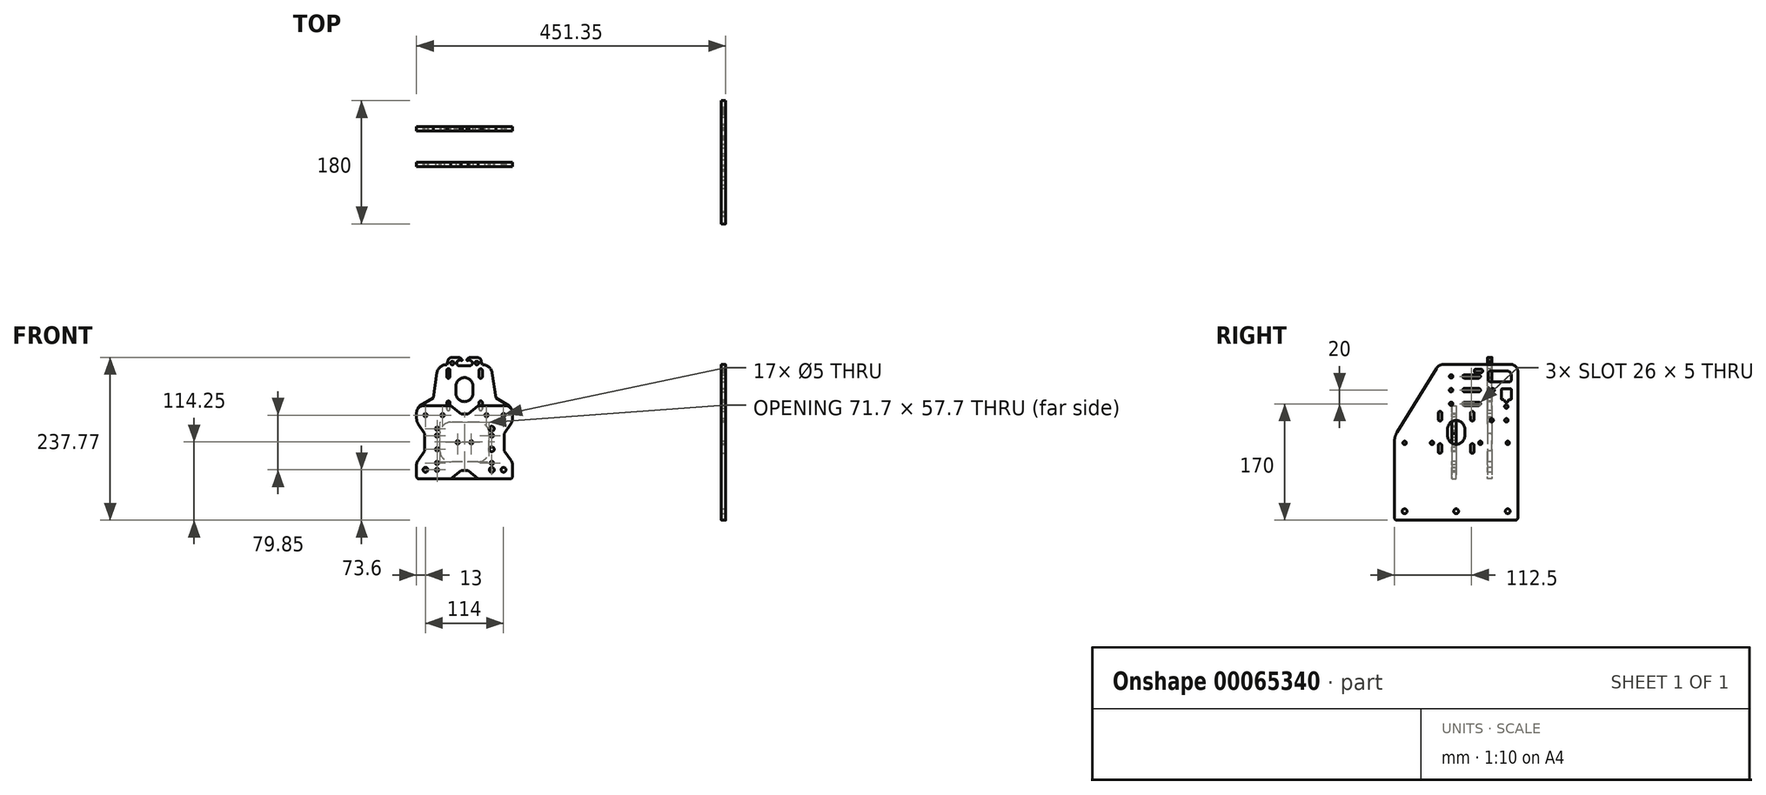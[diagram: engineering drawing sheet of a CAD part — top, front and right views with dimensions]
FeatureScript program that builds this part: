
annotation { "Feature Type Name" : "Feature", "Feature Type Description" : "" }
export const myFeature = defineFeature(function(context is Context, id is Id, definition is map)
    precondition{}
    {
        {
            var Q0;
            Q0=qCreatedBy(makeId("Right.planeOp"),FACE);
            var sketch = newSketch(context, id + "F0", { "sketchPlane" : qUnion([Q0])});
            skLineSegment(sketch, "E0", {"start": v(-28.77, 108.05) * mm, "end": v(-86.28, 14.78) * mm});
            skLineSegment(sketch, "E1", {"start": v(-90, 1.66) * mm, "end": v(-90, -110.25) * mm});
            skLineSegment(sketch, "E2", {"start": v(-86.5, -113.75) * mm, "end": v(86.5, -113.75) * mm});
            skLineSegment(sketch, "E3", {"start": v(90, -110.25) * mm, "end": v(90, 103.75) * mm});
            skLineSegment(sketch, "E4", {"start": v(80, 113.75) * mm, "end": v(-18.55, 113.75) * mm});
            skLineSegment(sketch, "E5", {"start": v(0, -113.75) * mm, "end": v(0, 0) * mm, "construction": true});
            skLineSegment(sketch, "E6", {"start": v(0, 0) * mm, "end": v(0, 113.75) * mm, "construction": true});
            skPoint(sketch, "E7.visualSharp", {"position": v(-25.25, 113.75) * mm});
            skArc(sketch, "E7.filletArc", {"start": v(-18.55, 113.75) * mm, "mid": v(-24.4, 112.23) * mm, "end": v(-28.77, 108.05) * mm});
            skPoint(sketch, "E8.visualSharp", {"position": v(90, 113.75) * mm});
            skArc(sketch, "E8.filletArc", {"start": v(90, 103.75) * mm, "mid": v(87.07, 110.82) * mm, "end": v(80, 113.75) * mm});
            skPoint(sketch, "E9.visualSharp", {"position": v(-90, -113.75) * mm});
            skArc(sketch, "E9.filletArc", {"start": v(-90, -110.25) * mm, "mid": v(-88.97, -112.72) * mm, "end": v(-86.5, -113.75) * mm});
            skPoint(sketch, "E10.visualSharp", {"position": v(90, -113.75) * mm});
            skArc(sketch, "E10.filletArc", {"start": v(86.5, -113.75) * mm, "mid": v(88.97, -112.72) * mm, "end": v(90, -110.25) * mm});
            skPoint(sketch, "E11.visualSharp", {"position": v(-90, 8.75) * mm});
            skArc(sketch, "E11.filletArc", {"start": v(-86.28, 14.78) * mm, "mid": v(-89.05, 8.48) * mm, "end": v(-90, 1.66) * mm});
            skSolve(sketch);
        }
        {
            var Q0;
            Q0=qSketchRegion(id+"F0",true);
            extrude(context, id + "F1", {"entities" : qUnion([Q0]), "depth" : 6.35 * mm});
        }
        {
            var Q0;
            Q0=makeQuery(id+"F1.opExtrude","CAP_FACE",FACE,{"disambiguationData":[OSD([sQuery(id+"F0.wireOp",EDGE,"E0"),sQuery(id+"F0.wireOp",EDGE,"E1"),sQuery(id+"F0.wireOp",EDGE,"E2"),sQuery(id+"F0.wireOp",EDGE,"E3"),sQuery(id+"F0.wireOp",EDGE,"E4"),sQuery(id+"F0.wireOp",EDGE,"E7.filletArc"),sQuery(id+"F0.wireOp",EDGE,"E8.filletArc"),sQuery(id+"F0.wireOp",EDGE,"E9.filletArc"),sQuery(id+"F0.wireOp",EDGE,"E10.filletArc"),sQuery(id+"F0.wireOp",EDGE,"E11.filletArc")])],"isStart":false});
            var sketch = newSketch(context, id + "F2", { "sketchPlane" : qUnion([Q0])});
            skLineSegment(sketch, "E12", {"start": v(0, 0) * mm, "end": v(0, -100.75) * mm, "construction": true});
            skLineSegment(sketch, "E13", {"start": v(0, -100.75) * mm, "end": v(75.3, -100.75) * mm, "construction": true});
            skLineSegment(sketch, "E14", {"start": v(0, -100.75) * mm, "end": v(-75.3, -100.75) * mm, "construction": true});
            skCircle(sketch, "E15", {"center": v(-75.3, -100.75) * mm, "radius": 3.57 * mm});
            skCircle(sketch, "E16", {"center": v(75.3, -100.75) * mm, "radius": 3.57 * mm});
            skCircle(sketch, "E17", {"center": v(0, -100.75) * mm, "radius": 3.57 * mm});
            skLineSegment(sketch, "E18", {"start": v(-75.3, -0.75) * mm, "end": v(-35.3, -0.75) * mm, "construction": true});
            skLineSegment(sketch, "E19", {"start": v(-35.3, -0.75) * mm, "end": v(0, -0.75) * mm, "construction": true});
            skLineSegment(sketch, "E20", {"start": v(0, -0.75) * mm, "end": v(35.3, -0.75) * mm, "construction": true});
            skLineSegment(sketch, "E21", {"start": v(35.3, -0.75) * mm, "end": v(75.3, -0.75) * mm, "construction": true});
            skCircle(sketch, "E22", {"center": v(-75.3, -0.75) * mm, "radius": 2.5 * mm});
            skCircle(sketch, "E23", {"center": v(-35.3, -0.75) * mm, "radius": 2.5 * mm});
            skCircle(sketch, "E24", {"center": v(35.3, -0.75) * mm, "radius": 2.5 * mm});
            skCircle(sketch, "E25", {"center": v(75.3, -0.75) * mm, "radius": 2.5 * mm});
            skLineSegment(sketch, "E26", {"start": v(-75.3, -0.75) * mm, "end": v(-75.3, -100.75) * mm, "construction": true});
            skLineSegment(sketch, "E27", {"start": v(75.3, -0.75) * mm, "end": v(75.3, -100.75) * mm, "construction": true});
            skSolve(sketch);
        }
        {
            var Q0;
            Q0=qSketchRegion(id+"F2",true);
            extrude(context, id + "F3", {"entities" : qUnion([Q0]), "operationType" : NewBodyOperationType.REMOVE, "endBound" : BoundingType.THROUGH_ALL, "oppositeDirection" : true, "depth" : 25 * mm});
        }
        {
            var Q0;
            Q0=makeQuery(id+"F1.opExtrude","CAP_FACE",FACE,{"disambiguationData":[OSD([sQuery(id+"F0.wireOp",EDGE,"E0"),sQuery(id+"F0.wireOp",EDGE,"E1"),sQuery(id+"F0.wireOp",EDGE,"E2"),sQuery(id+"F0.wireOp",EDGE,"E3"),sQuery(id+"F0.wireOp",EDGE,"E4"),sQuery(id+"F0.wireOp",EDGE,"E7.filletArc"),sQuery(id+"F0.wireOp",EDGE,"E8.filletArc"),sQuery(id+"F0.wireOp",EDGE,"E9.filletArc"),sQuery(id+"F0.wireOp",EDGE,"E10.filletArc"),sQuery(id+"F0.wireOp",EDGE,"E11.filletArc")])],"isStart":false});
            var sketch = newSketch(context, id + "F4", { "sketchPlane" : qUnion([Q0])});
            skArc(sketch, "E28", {"start": v(-12.5, 9.55) * mm, "mid": v(0, -2.95) * mm, "end": v(12.5, 9.55) * mm});
            skLineSegment(sketch, "E29", {"start": v(-12.5, 9.55) * mm, "end": v(-12.5, 19.55) * mm});
            skLineSegment(sketch, "E30", {"start": v(12.5, 19.55) * mm, "end": v(12.5, 9.55) * mm});
            skArc(sketch, "E31", {"start": v(-12.5, 19.55) * mm, "mid": v(0, 32.05) * mm, "end": v(12.5, 19.55) * mm});
            skLineSegment(sketch, "E32", {"start": v(0, 19.55) * mm, "end": v(0, 9.55) * mm, "construction": true});
            skLineSegment(sketch, "E33", {"start": v(-35.3, -0.75) * mm, "end": v(35.3, -0.75) * mm, "construction": true});
            skLineSegment(sketch, "E34", {"start": v(-23.57, 42.62) * mm, "end": v(-23.57, 33.62) * mm, "construction": true});
            skArc(sketch, "E35", {"start": v(-21.02, 42.62) * mm, "mid": v(-23.57, 45.17) * mm, "end": v(-26.12, 42.62) * mm});
            skArc(sketch, "E36", {"start": v(-26.12, 33.62) * mm, "mid": v(-23.57, 31.07) * mm, "end": v(-21.02, 33.62) * mm});
            skLineSegment(sketch, "E37", {"start": v(-21.02, 42.62) * mm, "end": v(-21.02, 33.62) * mm});
            skLineSegment(sketch, "E38", {"start": v(-26.12, 33.62) * mm, "end": v(-26.12, 42.62) * mm});
            skLineSegment(sketch, "E39", {"start": v(-12.5, 14.55) * mm, "end": v(12.5, 14.55) * mm, "construction": true});
            skLineSegment(sketch, "E40.MirrorCS", {"start": v(23.57, 42.62) * mm, "end": v(23.57, 33.62) * mm, "construction": true});
            skArc(sketch, "E41.MirrorCS", {"start": v(26.12, 33.62) * mm, "mid": v(23.57, 31.07) * mm, "end": v(21.02, 33.62) * mm});
            skLineSegment(sketch, "E42.MirrorCS", {"start": v(21.02, 42.62) * mm, "end": v(21.02, 33.62) * mm});
            skArc(sketch, "E43.MirrorCS", {"start": v(21.02, 42.62) * mm, "mid": v(23.57, 45.17) * mm, "end": v(26.12, 42.62) * mm});
            skLineSegment(sketch, "E44.MirrorCS", {"start": v(26.12, 33.62) * mm, "end": v(26.12, 42.62) * mm});
            skArc(sketch, "E45.MirrorCS", {"start": v(26.12, -4.52) * mm, "mid": v(23.57, -1.97) * mm, "end": v(21.02, -4.52) * mm});
            skLineSegment(sketch, "E46.MirrorCS", {"start": v(26.12, -4.52) * mm, "end": v(26.12, -13.52) * mm});
            skLineSegment(sketch, "E47.MirrorCS", {"start": v(-23.57, -13.52) * mm, "end": v(-23.57, -4.52) * mm, "construction": true});
            skLineSegment(sketch, "E48.MirrorCS", {"start": v(23.57, -13.52) * mm, "end": v(23.57, -4.52) * mm, "construction": true});
            skArc(sketch, "E49.MirrorCS", {"start": v(21.02, -13.52) * mm, "mid": v(23.57, -16.07) * mm, "end": v(26.12, -13.52) * mm});
            skLineSegment(sketch, "E50.MirrorCS", {"start": v(21.02, -13.52) * mm, "end": v(21.02, -4.52) * mm});
            skArc(sketch, "E51.MirrorCS", {"start": v(-26.12, -4.52) * mm, "mid": v(-23.57, -1.97) * mm, "end": v(-21.02, -4.52) * mm});
            skLineSegment(sketch, "E52.MirrorCS", {"start": v(-21.02, -13.52) * mm, "end": v(-21.02, -4.52) * mm});
            skArc(sketch, "E53.MirrorCS", {"start": v(-21.02, -13.52) * mm, "mid": v(-23.57, -16.07) * mm, "end": v(-26.12, -13.52) * mm});
            skLineSegment(sketch, "E54.MirrorCS", {"start": v(-26.12, -4.52) * mm, "end": v(-26.12, -13.52) * mm});
            skLineSegment(sketch, "E55", {"start": v(-23.57, 38.12) * mm, "end": v(23.57, -9.02) * mm, "construction": true});
            skLineSegment(sketch, "E56", {"start": v(23.57, -9.02) * mm, "end": v(-23.57, -9.02) * mm, "construction": true});
            skLineSegment(sketch, "E57", {"start": v(-23.57, -9.02) * mm, "end": v(23.57, 38.12) * mm, "construction": true});
            skSolve(sketch);
        }
        {
            var Q0;
            Q0=qSketchRegion(id+"F4",true);
            extrude(context, id + "F5", {"entities" : qUnion([Q0]), "operationType" : NewBodyOperationType.REMOVE, "endBound" : BoundingType.THROUGH_ALL, "oppositeDirection" : true, "depth" : 25 * mm});
        }
        {
            var Q0;
            Q0=makeQuery(id+"F1.opExtrude","CAP_FACE",FACE,{"disambiguationData":[OSD([sQuery(id+"F0.wireOp",EDGE,"E0"),sQuery(id+"F0.wireOp",EDGE,"E1"),sQuery(id+"F0.wireOp",EDGE,"E2"),sQuery(id+"F0.wireOp",EDGE,"E3"),sQuery(id+"F0.wireOp",EDGE,"E4"),sQuery(id+"F0.wireOp",EDGE,"E7.filletArc"),sQuery(id+"F0.wireOp",EDGE,"E8.filletArc"),sQuery(id+"F0.wireOp",EDGE,"E9.filletArc"),sQuery(id+"F0.wireOp",EDGE,"E10.filletArc"),sQuery(id+"F0.wireOp",EDGE,"E11.filletArc")])],"isStart":false});
            var sketch = newSketch(context, id + "F6", { "sketchPlane" : qUnion([Q0])});
            skCircle(sketch, "E58", {"center": v(-7.35, 96.25) * mm, "radius": 2.5 * mm});
            skLineSegment(sketch, "E59", {"start": v(-7.35, 96.25) * mm, "end": v(12, 96.25) * mm, "construction": true});
            skLineSegment(sketch, "E60", {"start": v(12, 96.25) * mm, "end": v(33, 96.25) * mm, "construction": true});
            skArc(sketch, "E61", {"start": v(12, 93.75) * mm, "mid": v(9.5, 96.25) * mm, "end": v(12, 98.75) * mm});
            skArc(sketch, "E62", {"start": v(33, 98.75) * mm, "mid": v(35.5, 96.25) * mm, "end": v(33, 93.75) * mm});
            skLineSegment(sketch, "E63", {"start": v(12, 98.75) * mm, "end": v(33, 98.75) * mm});
            skLineSegment(sketch, "E64", {"start": v(12, 93.75) * mm, "end": v(33, 93.75) * mm});
            skCircle(sketch, "E65.0.1.0", {"center": v(-7.35, 76.25) * mm, "radius": 2.5 * mm});
            skLineSegment(sketch, "E65.0.1.1", {"start": v(-7.35, 76.25) * mm, "end": v(12, 76.25) * mm, "construction": true});
            skArc(sketch, "E65.0.1.2", {"start": v(12, 73.75) * mm, "mid": v(9.5, 76.25) * mm, "end": v(12, 78.75) * mm});
            skLineSegment(sketch, "E65.0.1.3", {"start": v(12, 78.75) * mm, "end": v(33, 78.75) * mm});
            skLineSegment(sketch, "E65.0.1.4", {"start": v(12, 73.75) * mm, "end": v(33, 73.75) * mm});
            skArc(sketch, "E65.0.1.5", {"start": v(33, 78.75) * mm, "mid": v(35.5, 76.25) * mm, "end": v(33, 73.75) * mm});
            skCircle(sketch, "E65.0.2.0", {"center": v(-7.35, 56.25) * mm, "radius": 2.5 * mm});
            skLineSegment(sketch, "E65.0.2.1", {"start": v(-7.35, 56.25) * mm, "end": v(12, 56.25) * mm, "construction": true});
            skArc(sketch, "E65.0.2.2", {"start": v(12, 53.75) * mm, "mid": v(9.5, 56.25) * mm, "end": v(12, 58.75) * mm});
            skLineSegment(sketch, "E65.0.2.3", {"start": v(12, 58.75) * mm, "end": v(33, 58.75) * mm});
            skLineSegment(sketch, "E65.0.2.4", {"start": v(12, 53.75) * mm, "end": v(33, 53.75) * mm});
            skArc(sketch, "E65.0.2.5", {"start": v(33, 58.75) * mm, "mid": v(35.5, 56.25) * mm, "end": v(33, 53.75) * mm});
            skLineSegment(sketch, "E65.direction1", {"start": v(-7.35, 96.25) * mm, "end": v(-7.35, 96.25) * mm});
            skLineSegment(sketch, "E65.direction2", {"start": v(-7.35, 96.25) * mm, "end": v(-7.35, 76.25) * mm, "construction": true});
            skLineSegment(sketch, "E66", {"start": v(33, 76.25) * mm, "end": v(12, 76.25) * mm, "construction": true});
            skLineSegment(sketch, "E67", {"start": v(12, 56.25) * mm, "end": v(33, 56.25) * mm, "construction": true});
            skLineSegment(sketch, "E68", {"start": v(33, 76.25) * mm, "end": v(53.35, 76.25) * mm, "construction": true});
            skPoint(sketch, "E68.endSnap0", {"position": v(35.5, 76.25) * mm});
            skCircle(sketch, "E69", {"center": v(53.35, 76.25) * mm, "radius": 2.5 * mm});
            skSolve(sketch);
        }
        {
            var Q0;
            Q0=qSketchRegion(id+"F6",true);
            extrude(context, id + "F7", {"entities" : qUnion([Q0]), "operationType" : NewBodyOperationType.REMOVE, "endBound" : BoundingType.THROUGH_ALL, "oppositeDirection" : true, "depth" : 25 * mm});
        }
        {
            var Q0;
            Q0=makeQuery(id+"F1.opExtrude","CAP_FACE",FACE,{"disambiguationData":[OSD([sQuery(id+"F0.wireOp",EDGE,"E0"),sQuery(id+"F0.wireOp",EDGE,"E1"),sQuery(id+"F0.wireOp",EDGE,"E2"),sQuery(id+"F0.wireOp",EDGE,"E3"),sQuery(id+"F0.wireOp",EDGE,"E4"),sQuery(id+"F0.wireOp",EDGE,"E7.filletArc"),sQuery(id+"F0.wireOp",EDGE,"E8.filletArc"),sQuery(id+"F0.wireOp",EDGE,"E9.filletArc"),sQuery(id+"F0.wireOp",EDGE,"E10.filletArc"),sQuery(id+"F0.wireOp",EDGE,"E11.filletArc")])],"isStart":false});
            var sketch = newSketch(context, id + "F8", { "sketchPlane" : qUnion([Q0])});
            skLineSegment(sketch, "E70", {"start": v(12, 96.25) * mm, "end": v(33, 96.25) * mm, "construction": true});
            skLineSegment(sketch, "E71.bottom", {"start": v(28.1, 106.75) * mm, "end": v(36.9, 106.75) * mm});
            skLineSegment(sketch, "E71.top", {"start": v(28.1, 101.75) * mm, "end": v(36.9, 101.75) * mm});
            skLineSegment(sketch, "E71.left", {"start": v(26.5, 105.15) * mm, "end": v(26.5, 103.35) * mm});
            skLineSegment(sketch, "E71.right", {"start": v(38.5, 105.15) * mm, "end": v(38.5, 103.35) * mm});
            skPoint(sketch, "E72.visualSharp", {"position": v(26.5, 101.75) * mm});
            skArc(sketch, "E72.filletArc", {"start": v(26.5, 103.35) * mm, "mid": v(26.97, 102.22) * mm, "end": v(28.1, 101.75) * mm});
            skPoint(sketch, "E73.visualSharp", {"position": v(26.5, 106.75) * mm});
            skArc(sketch, "E73.filletArc", {"start": v(28.1, 106.75) * mm, "mid": v(26.97, 106.28) * mm, "end": v(26.5, 105.15) * mm});
            skPoint(sketch, "E74.visualSharp", {"position": v(38.5, 106.75) * mm});
            skArc(sketch, "E74.filletArc", {"start": v(38.5, 105.15) * mm, "mid": v(38.03, 106.28) * mm, "end": v(36.9, 106.75) * mm});
            skPoint(sketch, "E75.visualSharp", {"position": v(38.5, 101.75) * mm});
            skArc(sketch, "E75.filletArc", {"start": v(36.9, 101.75) * mm, "mid": v(38.03, 102.22) * mm, "end": v(38.5, 103.35) * mm});
            skLineSegment(sketch, "E76", {"start": v(26.5, 104.25) * mm, "end": v(38.5, 104.25) * mm, "construction": true});
            skLineSegment(sketch, "E77", {"start": v(32.5, 106.75) * mm, "end": v(32.5, 101.75) * mm, "construction": true});
            skLineSegment(sketch, "E78", {"start": v(22.5, 96.25) * mm, "end": v(22.5, 56.25) * mm, "construction": true});
            skPoint(sketch, "E78.endSnap0", {"position": v(22.5, 58.75) * mm});
            skLineSegment(sketch, "E79", {"start": v(12, 56.25) * mm, "end": v(33, 56.25) * mm, "construction": true});
            skSolve(sketch);
        }
        {
            var Q0;
            Q0=qSketchRegion(id+"F8",true);
            extrude(context, id + "F9", {"entities" : qUnion([Q0]), "operationType" : NewBodyOperationType.REMOVE, "endBound" : BoundingType.THROUGH_ALL, "oppositeDirection" : true, "depth" : 25 * mm});
        }
        {
            var Q0;
            Q0=makeQuery(id+"F1.opExtrude","CAP_FACE",FACE,{"disambiguationData":[OSD([sQuery(id+"F0.wireOp",EDGE,"E0"),sQuery(id+"F0.wireOp",EDGE,"E1"),sQuery(id+"F0.wireOp",EDGE,"E2"),sQuery(id+"F0.wireOp",EDGE,"E3"),sQuery(id+"F0.wireOp",EDGE,"E4"),sQuery(id+"F0.wireOp",EDGE,"E7.filletArc"),sQuery(id+"F0.wireOp",EDGE,"E8.filletArc"),sQuery(id+"F0.wireOp",EDGE,"E9.filletArc"),sQuery(id+"F0.wireOp",EDGE,"E10.filletArc"),sQuery(id+"F0.wireOp",EDGE,"E11.filletArc")])],"isStart":false});
            var sketch = newSketch(context, id + "F10", { "sketchPlane" : qUnion([Q0])});
            skCircle(sketch, "E80", {"center": v(73.3, 52.25) * mm, "radius": 2.5 * mm});
            skLineSegment(sketch, "E81", {"start": v(73.3, 52.25) * mm, "end": v(73.3, 32.25) * mm, "construction": true});
            skCircle(sketch, "E82", {"center": v(73.3, 32.25) * mm, "radius": 2.5 * mm});
            skLineSegment(sketch, "E83", {"start": v(73.3, 32.25) * mm, "end": v(51.95, 32.25) * mm, "construction": true});
            skCircle(sketch, "E84", {"center": v(51.95, 32.25) * mm, "radius": 2.5 * mm});
            skLineSegment(sketch, "E85", {"start": v(12, 56.25) * mm, "end": v(33, 56.25) * mm, "construction": true});
            skLineSegment(sketch, "E86", {"start": v(33, 56.25) * mm, "end": v(33, 52.25) * mm, "construction": true});
            skLineSegment(sketch, "E87", {"start": v(33, 52.25) * mm, "end": v(73.3, 52.25) * mm, "construction": true});
            skSolve(sketch);
        }
        {
            var Q0;
            Q0=qSketchRegion(id+"F10",true);
            extrude(context, id + "F11", {"entities" : qUnion([Q0]), "operationType" : NewBodyOperationType.REMOVE, "endBound" : BoundingType.THROUGH_ALL, "oppositeDirection" : true, "depth" : 25 * mm});
        }
        {
            var Q0;
            Q0=makeQuery(id+"F1.opExtrude","CAP_FACE",FACE,{"disambiguationData":[OSD([sQuery(id+"F0.wireOp",EDGE,"E0"),sQuery(id+"F0.wireOp",EDGE,"E1"),sQuery(id+"F0.wireOp",EDGE,"E2"),sQuery(id+"F0.wireOp",EDGE,"E3"),sQuery(id+"F0.wireOp",EDGE,"E4"),sQuery(id+"F0.wireOp",EDGE,"E7.filletArc"),sQuery(id+"F0.wireOp",EDGE,"E8.filletArc"),sQuery(id+"F0.wireOp",EDGE,"E9.filletArc"),sQuery(id+"F0.wireOp",EDGE,"E10.filletArc"),sQuery(id+"F0.wireOp",EDGE,"E11.filletArc")])],"isStart":false});
            var sketch = newSketch(context, id + "F12", { "sketchPlane" : qUnion([Q0])});
            skLineSegment(sketch, "E88", {"start": v(65.95, 76.8) * mm, "end": v(65.95, 63.85) * mm});
            skLineSegment(sketch, "E89", {"start": v(67.55, 62.25) * mm, "end": v(69.65, 62.25) * mm});
            skLineSegment(sketch, "E90", {"start": v(69.65, 62.25) * mm, "end": v(70.8, 60.75) * mm});
            skLineSegment(sketch, "E91", {"start": v(75.8, 60.75) * mm, "end": v(76.95, 62.25) * mm});
            skLineSegment(sketch, "E92", {"start": v(76.95, 62.25) * mm, "end": v(79.05, 62.25) * mm});
            skLineSegment(sketch, "E93", {"start": v(80.65, 63.85) * mm, "end": v(80.65, 76.8) * mm});
            skLineSegment(sketch, "E94", {"start": v(79.05, 78.4) * mm, "end": v(67.55, 78.4) * mm});
            skArc(sketch, "E95", {"start": v(70.8, 60.75) * mm, "mid": v(73.3, 58.25) * mm, "end": v(75.8, 60.75) * mm});
            skLineSegment(sketch, "E96", {"start": v(73.3, 60.75) * mm, "end": v(73.3, 52.25) * mm, "construction": true});
            skLineSegment(sketch, "E97", {"start": v(73.3, 78.4) * mm, "end": v(73.3, 60.75) * mm, "construction": true});
            skLineSegment(sketch, "E98", {"start": v(65.95, 70.32) * mm, "end": v(80.65, 70.32) * mm, "construction": true});
            skPoint(sketch, "E99.visualSharp", {"position": v(65.95, 62.25) * mm});
            skArc(sketch, "E99.filletArc", {"start": v(65.95, 63.85) * mm, "mid": v(66.42, 62.72) * mm, "end": v(67.55, 62.25) * mm});
            skPoint(sketch, "E100.visualSharp", {"position": v(65.95, 78.4) * mm});
            skArc(sketch, "E100.filletArc", {"start": v(67.55, 78.4) * mm, "mid": v(66.42, 77.93) * mm, "end": v(65.95, 76.8) * mm});
            skPoint(sketch, "E101.visualSharp", {"position": v(80.65, 78.4) * mm});
            skArc(sketch, "E101.filletArc", {"start": v(80.65, 76.8) * mm, "mid": v(80.18, 77.93) * mm, "end": v(79.05, 78.4) * mm});
            skPoint(sketch, "E102.visualSharp", {"position": v(80.65, 62.25) * mm});
            skArc(sketch, "E102.filletArc", {"start": v(79.05, 62.25) * mm, "mid": v(80.18, 62.72) * mm, "end": v(80.65, 63.85) * mm});
            skLineSegment(sketch, "E103", {"start": v(80.65, 91.4) * mm, "end": v(80.65, 97.6) * mm});
            skLineSegment(sketch, "E104", {"start": v(74, 104.25) * mm, "end": v(50.3, 104.25) * mm});
            skLineSegment(sketch, "E105", {"start": v(47.15, 101.1) * mm, "end": v(47.15, 91.4) * mm});
            skLineSegment(sketch, "E106", {"start": v(50.3, 88.25) * mm, "end": v(77.5, 88.25) * mm});
            skPoint(sketch, "E107.visualSharp", {"position": v(80.65, 104.25) * mm});
            skArc(sketch, "E107.filletArc", {"start": v(80.65, 97.6) * mm, "mid": v(78.7, 102.3) * mm, "end": v(74, 104.25) * mm});
            skPoint(sketch, "E108.visualSharp", {"position": v(80.65, 88.25) * mm});
            skArc(sketch, "E108.filletArc", {"start": v(77.5, 88.25) * mm, "mid": v(79.73, 89.17) * mm, "end": v(80.65, 91.4) * mm});
            skPoint(sketch, "E109.visualSharp", {"position": v(47.15, 88.25) * mm});
            skArc(sketch, "E109.filletArc", {"start": v(47.15, 91.4) * mm, "mid": v(48.07, 89.17) * mm, "end": v(50.3, 88.25) * mm});
            skPoint(sketch, "E110.visualSharp", {"position": v(47.15, 104.25) * mm});
            skArc(sketch, "E110.filletArc", {"start": v(50.3, 104.25) * mm, "mid": v(48.07, 103.33) * mm, "end": v(47.15, 101.1) * mm});
            skSolve(sketch);
        }
        {
            var Q0;
            Q0=qSketchRegion(id+"F12",true);
            extrude(context, id + "F13", {"entities" : qUnion([Q0]), "operationType" : NewBodyOperationType.REMOVE, "endBound" : BoundingType.THROUGH_ALL, "oppositeDirection" : true, "depth" : 25 * mm});
        }
        {
            var Q0;
            Q0=makeQuery(id+"F1.opExtrude","SWEPT_BODY",BODY,{"disambiguationData":[OSD([sQuery(id+"F0.wireOp",EDGE,"E0"),sQuery(id+"F0.wireOp",EDGE,"E1"),sQuery(id+"F0.wireOp",EDGE,"E2"),sQuery(id+"F0.wireOp",EDGE,"E3"),sQuery(id+"F0.wireOp",EDGE,"E4"),sQuery(id+"F0.wireOp",EDGE,"E7.filletArc"),sQuery(id+"F0.wireOp",EDGE,"E8.filletArc"),sQuery(id+"F0.wireOp",EDGE,"E9.filletArc"),sQuery(id+"F0.wireOp",EDGE,"E10.filletArc"),sQuery(id+"F0.wireOp",EDGE,"E11.filletArc")])]});
            transform(context, id + "F14", {"entities" : qUnion([Q0]), "transformType" : TransformType.TRANSLATION_3D, "dx" : (750 / 2) * mm, "dy" : 0 * mm, "dz" : 0 * mm, "makeCopy" : false});
        }
        {
            var Q0;
            Q0=qCreatedBy(makeId("Front.planeOp"),FACE);
            var sketch = newSketch(context, id + "F15", { "sketchPlane" : qUnion([Q0])});
            skLineSegment(sketch, "E111", {"start": v(0, 0) * mm, "end": v(0, 41.2) * mm, "construction": true});
            skLineSegment(sketch, "E112", {"start": v(0, 0) * mm, "end": v(0, -41.2) * mm, "construction": true});
            skLineSegment(sketch, "E113", {"start": v(0, 41.2) * mm, "end": v(5, 41.2) * mm});
            skLineSegment(sketch, "E114", {"start": v(20, 53.35) * mm, "end": v(5, 41.2) * mm});
            skLineSegment(sketch, "E115", {"start": v(20, 53.35) * mm, "end": v(70, 53.35) * mm});
            skLineSegment(sketch, "E116", {"start": v(70, 53.35) * mm, "end": v(70, 30.5) * mm});
            skLineSegment(sketch, "E117", {"start": v(70, 30.5) * mm, "end": v(58, 12.75) * mm});
            skLineSegment(sketch, "E118", {"start": v(58, 12.75) * mm, "end": v(58, -12.75) * mm});
            skLineSegment(sketch, "E119", {"start": v(58, -12.75) * mm, "end": v(70, -29.25) * mm});
            skLineSegment(sketch, "E120", {"start": v(70, -29.25) * mm, "end": v(70, -53.35) * mm});
            skLineSegment(sketch, "E121", {"start": v(70, -53.35) * mm, "end": v(20, -53.35) * mm});
            skLineSegment(sketch, "E122", {"start": v(20, -53.35) * mm, "end": v(5, -41.2) * mm});
            skLineSegment(sketch, "E123", {"start": v(5, -41.2) * mm, "end": v(0, -41.2) * mm});
            skLineSegment(sketch, "E124", {"start": v(20, 53.35) * mm, "end": v(20, -53.35) * mm, "construction": true});
            skLineSegment(sketch, "E125", {"start": v(0, 41.2) * mm, "end": v(0, 53.35) * mm, "construction": true});
            skLineSegment(sketch, "E126", {"start": v(0, 53.35) * mm, "end": v(20, 53.35) * mm, "construction": true});
            skLineSegment(sketch, "E127", {"start": v(0, -41.2) * mm, "end": v(0, -53.35) * mm, "construction": true});
            skLineSegment(sketch, "E128", {"start": v(0, -53.35) * mm, "end": v(20, -53.35) * mm, "construction": true});
            skLineSegment(sketch, "E129", {"start": v(5, 41.2) * mm, "end": v(5, -41.2) * mm, "construction": true});
            skLineSegment(sketch, "E130", {"start": v(0, 0) * mm, "end": v(58, 0) * mm, "construction": true});
            skLineSegment(sketch, "E131", {"start": v(70, 30.5) * mm, "end": v(70, -29.25) * mm, "construction": true});
            skLineSegment(sketch, "E132.MirrorCS", {"start": v(-5, -41.2) * mm, "end": v(0, -41.2) * mm});
            skLineSegment(sketch, "E133.MirrorCS", {"start": v(-20, -53.35) * mm, "end": v(-5, -41.2) * mm});
            skLineSegment(sketch, "E134.MirrorCS", {"start": v(-70, -53.35) * mm, "end": v(-20, -53.35) * mm});
            skLineSegment(sketch, "E135.MirrorCS", {"start": v(-70, -29.25) * mm, "end": v(-70, -53.35) * mm});
            skLineSegment(sketch, "E136.MirrorCS", {"start": v(-58, -12.75) * mm, "end": v(-70, -29.25) * mm});
            skLineSegment(sketch, "E137.MirrorCS", {"start": v(-58, 12.75) * mm, "end": v(-58, -12.75) * mm});
            skLineSegment(sketch, "E138.MirrorCS", {"start": v(-70, 30.5) * mm, "end": v(-58, 12.75) * mm});
            skLineSegment(sketch, "E139.MirrorCS", {"start": v(-70, 53.35) * mm, "end": v(-70, 30.5) * mm});
            skLineSegment(sketch, "E140.MirrorCS", {"start": v(-20, 53.35) * mm, "end": v(-70, 53.35) * mm});
            skLineSegment(sketch, "E141.MirrorCS", {"start": v(0, 41.2) * mm, "end": v(-5, 41.2) * mm});
            skLineSegment(sketch, "E142.MirrorCS", {"start": v(-20, 53.35) * mm, "end": v(-5, 41.2) * mm});
            skSolve(sketch);
        }
        {
            var Q0;
            Q0=qSketchRegion(id+"F15",true);
            extrude(context, id + "F16", {"entities" : qUnion([Q0]), "depth" : 6.35 * mm});
        }
        {
            var Q0;
            Q0=makeQuery(id+"F16.opExtrude","CAP_FACE",FACE,{"disambiguationData":[OSD([sQuery(id+"F15.wireOp",EDGE,"E113"),sQuery(id+"F15.wireOp",EDGE,"E114"),sQuery(id+"F15.wireOp",EDGE,"E115"),sQuery(id+"F15.wireOp",EDGE,"E116"),sQuery(id+"F15.wireOp",EDGE,"E117"),sQuery(id+"F15.wireOp",EDGE,"E118"),sQuery(id+"F15.wireOp",EDGE,"E119"),sQuery(id+"F15.wireOp",EDGE,"E120"),sQuery(id+"F15.wireOp",EDGE,"E121"),sQuery(id+"F15.wireOp",EDGE,"E122"),sQuery(id+"F15.wireOp",EDGE,"E123"),sQuery(id+"F15.wireOp",EDGE,"E132.MirrorCS"),sQuery(id+"F15.wireOp",EDGE,"E133.MirrorCS"),sQuery(id+"F15.wireOp",EDGE,"E134.MirrorCS"),sQuery(id+"F15.wireOp",EDGE,"E135.MirrorCS"),sQuery(id+"F15.wireOp",EDGE,"E136.MirrorCS"),sQuery(id+"F15.wireOp",EDGE,"E137.MirrorCS"),sQuery(id+"F15.wireOp",EDGE,"E138.MirrorCS"),sQuery(id+"F15.wireOp",EDGE,"E139.MirrorCS"),sQuery(id+"F15.wireOp",EDGE,"E140.MirrorCS"),sQuery(id+"F15.wireOp",EDGE,"E141.MirrorCS"),sQuery(id+"F15.wireOp",EDGE,"E142.MirrorCS")])],"isStart":false});
            var sketch = newSketch(context, id + "F17", { "sketchPlane" : qUnion([Q0])});
            skLineSegment(sketch, "E143", {"start": v(0, 0) * mm, "end": v(10, 0) * mm, "construction": true});
            skLineSegment(sketch, "E144", {"start": v(0, 0) * mm, "end": v(-10, 0) * mm, "construction": true});
            skCircle(sketch, "E145", {"center": v(-10, 0) * mm, "radius": 2.5 * mm});
            skCircle(sketch, "E146", {"center": v(10, 0) * mm, "radius": 2.5 * mm});
            skSolve(sketch);
        }
        {
            var Q0;
            Q0=qSketchRegion(id+"F17",true);
            extrude(context, id + "F18", {"entities" : qUnion([Q0]), "operationType" : NewBodyOperationType.REMOVE, "endBound" : BoundingType.THROUGH_ALL, "oppositeDirection" : true, "depth" : 25 * mm});
        }
        {
            var Q0;
            Q0=makeQuery(id+"F16.opExtrude","CAP_FACE",FACE,{"disambiguationData":[OSD([sQuery(id+"F15.wireOp",EDGE,"E113"),sQuery(id+"F15.wireOp",EDGE,"E114"),sQuery(id+"F15.wireOp",EDGE,"E115"),sQuery(id+"F15.wireOp",EDGE,"E116"),sQuery(id+"F15.wireOp",EDGE,"E117"),sQuery(id+"F15.wireOp",EDGE,"E118"),sQuery(id+"F15.wireOp",EDGE,"E119"),sQuery(id+"F15.wireOp",EDGE,"E120"),sQuery(id+"F15.wireOp",EDGE,"E121"),sQuery(id+"F15.wireOp",EDGE,"E122"),sQuery(id+"F15.wireOp",EDGE,"E123"),sQuery(id+"F15.wireOp",EDGE,"E132.MirrorCS"),sQuery(id+"F15.wireOp",EDGE,"E133.MirrorCS"),sQuery(id+"F15.wireOp",EDGE,"E134.MirrorCS"),sQuery(id+"F15.wireOp",EDGE,"E135.MirrorCS"),sQuery(id+"F15.wireOp",EDGE,"E136.MirrorCS"),sQuery(id+"F15.wireOp",EDGE,"E137.MirrorCS"),sQuery(id+"F15.wireOp",EDGE,"E138.MirrorCS"),sQuery(id+"F15.wireOp",EDGE,"E139.MirrorCS"),sQuery(id+"F15.wireOp",EDGE,"E140.MirrorCS"),sQuery(id+"F15.wireOp",EDGE,"E141.MirrorCS"),sQuery(id+"F15.wireOp",EDGE,"E142.MirrorCS")])],"isStart":false});
            var sketch = newSketch(context, id + "F19", { "sketchPlane" : qUnion([Q0])});
            skLineSegment(sketch, "E147", {"start": v(0, 41.2) * mm, "end": v(0, -41.2) * mm, "construction": true});
            skLineSegment(sketch, "E148", {"start": v(32, 39.7) * mm, "end": v(57, 39.7) * mm, "construction": true});
            skCircle(sketch, "E149", {"center": v(32, 39.7) * mm, "radius": 2.5 * mm});
            skCircle(sketch, "E150", {"center": v(57, 39.7) * mm, "radius": 2.5 * mm});
            skCircle(sketch, "E151", {"center": v(57, -40.1) * mm, "radius": 3.57 * mm});
            skCircle(sketch, "E152.MirrorC", {"center": v(-57, -40.1) * mm, "radius": 3.57 * mm});
            skCircle(sketch, "E153.MirrorC", {"center": v(-57, 39.7) * mm, "radius": 2.5 * mm});
            skCircle(sketch, "E154.MirrorC", {"center": v(-32, 39.7) * mm, "radius": 2.5 * mm});
            skLineSegment(sketch, "E155", {"start": v(-57, 39.7) * mm, "end": v(-32, 39.7) * mm, "construction": true});
            skLineSegment(sketch, "E156", {"start": v(57, 39.7) * mm, "end": v(57, -40.1) * mm, "construction": true});
            skLineSegment(sketch, "E157", {"start": v(-57, 39.7) * mm, "end": v(-57, -40.1) * mm, "construction": true});
            skLineSegment(sketch, "E158", {"start": v(-57, -40.1) * mm, "end": v(57, -40.1) * mm, "construction": true});
            skLineSegment(sketch, "E159", {"start": v(-32, 39.7) * mm, "end": v(32, 39.7) * mm, "construction": true});
            skSolve(sketch);
        }
        {
            var Q0;
            Q0=qSketchRegion(id+"F19",true);
            extrude(context, id + "F20", {"entities" : qUnion([Q0]), "operationType" : NewBodyOperationType.REMOVE, "endBound" : BoundingType.THROUGH_ALL, "oppositeDirection" : true, "depth" : 25 * mm});
        }
        {
            var Q0;
            Q0=makeQuery(id+"F16.opExtrude","CAP_FACE",FACE,{"disambiguationData":[OSD([sQuery(id+"F15.wireOp",EDGE,"E113"),sQuery(id+"F15.wireOp",EDGE,"E114"),sQuery(id+"F15.wireOp",EDGE,"E115"),sQuery(id+"F15.wireOp",EDGE,"E116"),sQuery(id+"F15.wireOp",EDGE,"E117"),sQuery(id+"F15.wireOp",EDGE,"E118"),sQuery(id+"F15.wireOp",EDGE,"E119"),sQuery(id+"F15.wireOp",EDGE,"E120"),sQuery(id+"F15.wireOp",EDGE,"E121"),sQuery(id+"F15.wireOp",EDGE,"E122"),sQuery(id+"F15.wireOp",EDGE,"E123"),sQuery(id+"F15.wireOp",EDGE,"E132.MirrorCS"),sQuery(id+"F15.wireOp",EDGE,"E133.MirrorCS"),sQuery(id+"F15.wireOp",EDGE,"E134.MirrorCS"),sQuery(id+"F15.wireOp",EDGE,"E135.MirrorCS"),sQuery(id+"F15.wireOp",EDGE,"E136.MirrorCS"),sQuery(id+"F15.wireOp",EDGE,"E137.MirrorCS"),sQuery(id+"F15.wireOp",EDGE,"E138.MirrorCS"),sQuery(id+"F15.wireOp",EDGE,"E139.MirrorCS"),sQuery(id+"F15.wireOp",EDGE,"E140.MirrorCS"),sQuery(id+"F15.wireOp",EDGE,"E141.MirrorCS"),sQuery(id+"F15.wireOp",EDGE,"E142.MirrorCS")])],"isStart":false});
            var sketch = newSketch(context, id + "F21", { "sketchPlane" : qUnion([Q0])});
            skLineSegment(sketch, "E160", {"start": v(0, 41.2) * mm, "end": v(0, -41.2) * mm, "construction": true});
            skLineSegment(sketch, "E161", {"start": v(39.8, 9.85) * mm, "end": v(39.8, -10.15) * mm, "construction": true});
            skLineSegment(sketch, "E162", {"start": v(39.8, -10.15) * mm, "end": v(39.8, -30.15) * mm, "construction": true});
            skLineSegment(sketch, "E163", {"start": v(39.8, 9.85) * mm, "end": v(39.8, 19.85) * mm, "construction": true});
            skLineSegment(sketch, "E164", {"start": v(39.8, -30.15) * mm, "end": v(39.8, -40.15) * mm, "construction": true});
            skCircle(sketch, "E165", {"center": v(39.8, 19.85) * mm, "radius": 3.57 * mm});
            skCircle(sketch, "E166", {"center": v(39.8, -10.15) * mm, "radius": 3.57 * mm});
            skCircle(sketch, "E167", {"center": v(39.8, -40.15) * mm, "radius": 3.57 * mm});
            skCircle(sketch, "E168", {"center": v(39.8, 9.85) * mm, "radius": 2.5 * mm});
            skCircle(sketch, "E169", {"center": v(39.8, -30.15) * mm, "radius": 2.5 * mm});
            skLineSegment(sketch, "E170", {"start": v(39.8, -10.15) * mm, "end": v(0, -10.15) * mm, "construction": true});
            skLineSegment(sketch, "E171", {"start": v(-40, 9.85) * mm, "end": v(-40, 19.85) * mm, "construction": true});
            skLineSegment(sketch, "E172", {"start": v(-40, -30.15) * mm, "end": v(-40, -40.15) * mm, "construction": true});
            skCircle(sketch, "E173", {"center": v(-40, 19.85) * mm, "radius": 2.5 * mm});
            skCircle(sketch, "E174", {"center": v(-40, 9.85) * mm, "radius": 2.5 * mm});
            skCircle(sketch, "E175", {"center": v(-40, -10.15) * mm, "radius": 2.5 * mm});
            skCircle(sketch, "E176", {"center": v(-40, -30.15) * mm, "radius": 2.5 * mm});
            skCircle(sketch, "E177", {"center": v(-40, -40.15) * mm, "radius": 2.5 * mm});
            skLineSegment(sketch, "E178", {"start": v(-40, -30.15) * mm, "end": v(-40, -10.15) * mm, "construction": true});
            skLineSegment(sketch, "E179", {"start": v(-40, 9.85) * mm, "end": v(-40, -10.15) * mm, "construction": true});
            skLineSegment(sketch, "E180", {"start": v(-40, -10.15) * mm, "end": v(0, -10.15) * mm, "construction": true});
            skSolve(sketch);
        }
        {
            var Q0;
            Q0=qSketchRegion(id+"F21",true);
            extrude(context, id + "F22", {"entities" : qUnion([Q0]), "operationType" : NewBodyOperationType.REMOVE, "endBound" : BoundingType.THROUGH_ALL, "oppositeDirection" : true, "depth" : 25 * mm});
        }
        {
            var Q0;
            Q0=makeQuery(id+"F16.opExtrude","SWEPT_EDGE",EDGE,{"disambiguationData":[OSD([sQuery(id+"F15.wireOp",EDGE,"E139.MirrorCS"),sQuery(id+"F15.wireOp",EDGE,"E140.MirrorCS")])]});
            var Q1;
            Q1=makeQuery(id+"F16.opExtrude","SWEPT_EDGE",EDGE,{"disambiguationData":[OSD([sQuery(id+"F15.wireOp",EDGE,"E115"),sQuery(id+"F15.wireOp",EDGE,"E116")])]});
            fillet(context, id + "F23", {"entities" : qUnion([Q0, Q1]), "radius" : 9.6 * mm, "tangentPropagation" : true, "allowEdgeOverflow" : false});
        }
        {
            var Q0;
            Q0=makeQuery(id+"F16.opExtrude","SWEPT_EDGE",EDGE,{"disambiguationData":[OSD([sQuery(id+"F15.wireOp",EDGE,"E120"),sQuery(id+"F15.wireOp",EDGE,"E121")])]});
            var Q1;
            Q1=makeQuery(id+"F16.opExtrude","SWEPT_EDGE",EDGE,{"disambiguationData":[OSD([sQuery(id+"F15.wireOp",EDGE,"E134.MirrorCS"),sQuery(id+"F15.wireOp",EDGE,"E135.MirrorCS")])]});
            fillet(context, id + "F24", {"entities" : qUnion([Q0, Q1]), "radius" : 3.36 * mm, "tangentPropagation" : true, "allowEdgeOverflow" : false});
        }
        {
            var Q0;
            Q0=makeQuery(id+"F16.opExtrude","SWEPT_EDGE",EDGE,{"disambiguationData":[OSD([sQuery(id+"F15.wireOp",EDGE,"E116"),sQuery(id+"F15.wireOp",EDGE,"E117")])]});
            var Q1;
            Q1=makeQuery(id+"F16.opExtrude","SWEPT_EDGE",EDGE,{"disambiguationData":[OSD([sQuery(id+"F15.wireOp",EDGE,"E138.MirrorCS"),sQuery(id+"F15.wireOp",EDGE,"E139.MirrorCS")])]});
            fillet(context, id + "F25", {"entities" : qUnion([Q0, Q1]), "radius" : 14 * mm, "tangentPropagation" : true, "allowEdgeOverflow" : false});
        }
        {
            var Q0;
            Q0=makeQuery(id+"F16.opExtrude","SWEPT_EDGE",EDGE,{"disambiguationData":[OSD([sQuery(id+"F15.wireOp",EDGE,"E119"),sQuery(id+"F15.wireOp",EDGE,"E120")])]});
            var Q1;
            Q1=makeQuery(id+"F16.opExtrude","SWEPT_EDGE",EDGE,{"disambiguationData":[OSD([sQuery(id+"F15.wireOp",EDGE,"E135.MirrorCS"),sQuery(id+"F15.wireOp",EDGE,"E136.MirrorCS")])]});
            fillet(context, id + "F26", {"entities" : qUnion([Q0, Q1]), "radius" : 11 * mm, "tangentPropagation" : true, "allowEdgeOverflow" : false});
        }
        {
            var Q0;
            Q0=makeQuery(id+"F16.opExtrude","CAP_FACE",FACE,{"disambiguationData":[OSD([sQuery(id+"F15.wireOp",EDGE,"E113"),sQuery(id+"F15.wireOp",EDGE,"E114"),sQuery(id+"F15.wireOp",EDGE,"E115"),sQuery(id+"F15.wireOp",EDGE,"E116"),sQuery(id+"F15.wireOp",EDGE,"E117"),sQuery(id+"F15.wireOp",EDGE,"E118"),sQuery(id+"F15.wireOp",EDGE,"E119"),sQuery(id+"F15.wireOp",EDGE,"E120"),sQuery(id+"F15.wireOp",EDGE,"E121"),sQuery(id+"F15.wireOp",EDGE,"E122"),sQuery(id+"F15.wireOp",EDGE,"E123"),sQuery(id+"F15.wireOp",EDGE,"E132.MirrorCS"),sQuery(id+"F15.wireOp",EDGE,"E133.MirrorCS"),sQuery(id+"F15.wireOp",EDGE,"E134.MirrorCS"),sQuery(id+"F15.wireOp",EDGE,"E135.MirrorCS"),sQuery(id+"F15.wireOp",EDGE,"E136.MirrorCS"),sQuery(id+"F15.wireOp",EDGE,"E137.MirrorCS"),sQuery(id+"F15.wireOp",EDGE,"E138.MirrorCS"),sQuery(id+"F15.wireOp",EDGE,"E139.MirrorCS"),sQuery(id+"F15.wireOp",EDGE,"E140.MirrorCS"),sQuery(id+"F15.wireOp",EDGE,"E141.MirrorCS"),sQuery(id+"F15.wireOp",EDGE,"E142.MirrorCS")])],"isStart":true});
            cPlane(context, id + "F27", {"entities" : qUnion([Q0]), "cplaneType" : CPlaneType.OFFSET, "offset" : 46 * mm, "width" : 150 * mm, "height" : 150 * mm});
        }
        {
            var Q0;
            Q0=qCreatedBy(id+"F27.planeOp",FACE);
            var sketch = newSketch(context, id + "F28", { "sketchPlane" : qUnion([Q0])});
            skLineSegment(sketch, "E181", {"start": v(0, 0) * mm, "end": v(0, -53.35) * mm, "construction": true});
            skLineSegment(sketch, "E182", {"start": v(-67.5, 51.95) * mm, "end": v(-45.84, 64.81) * mm});
            skLineSegment(sketch, "E183", {"start": v(-45.84, 64.81) * mm, "end": v(-38.5, 113.35) * mm});
            skLineSegment(sketch, "E184", {"start": v(-38.5, 113.35) * mm, "end": v(-26, 113.35) * mm});
            skLineSegment(sketch, "E185", {"start": v(-26, 113.35) * mm, "end": v(-22.45, 124.02) * mm, "construction": true});
            skLineSegment(sketch, "E186", {"start": v(-22.45, 124.02) * mm, "end": v(0, 124.02) * mm, "construction": true});
            skLineSegment(sketch, "E187", {"start": v(0, 124.02) * mm, "end": v(0, 0) * mm, "construction": true});
            skLineSegment(sketch, "E188.MirrorCS", {"start": v(22.45, 124.02) * mm, "end": v(0, 124.02) * mm, "construction": true});
            skLineSegment(sketch, "E189.MirrorCS", {"start": v(26, 113.35) * mm, "end": v(22.45, 124.02) * mm, "construction": true});
            skLineSegment(sketch, "E190.MirrorCS", {"start": v(38.5, 113.35) * mm, "end": v(26, 113.35) * mm});
            skLineSegment(sketch, "E191.MirrorCS", {"start": v(45.84, 64.81) * mm, "end": v(38.5, 113.35) * mm});
            skLineSegment(sketch, "E192.MirrorCS", {"start": v(67.5, 51.95) * mm, "end": v(45.84, 64.81) * mm});
            skLineSegment(sketch, "E193", {"start": v(45.84, 64.81) * mm, "end": v(45.84, 113.35) * mm, "construction": true});
            skArc(sketch, "E194.0", {"start": v(70, 34.79) * mm, "mid": v(69.39, 30.69) * mm, "end": v(67.6, 26.95) * mm});
            skLineSegment(sketch, "E195.0", {"start": v(67.6, 26.95) * mm, "end": v(58, 12.75) * mm});
            skLineSegment(sketch, "E196.0", {"start": v(58, 12.75) * mm, "end": v(58, -12.75) * mm});
            skLineSegment(sketch, "E197.0", {"start": v(58, -12.75) * mm, "end": v(67.9, -26.36) * mm});
            skArc(sketch, "E198.0", {"start": v(67.9, -26.36) * mm, "mid": v(69.46, -29.43) * mm, "end": v(70, -32.83) * mm});
            skLineSegment(sketch, "E199.0", {"start": v(70, -32.83) * mm, "end": v(70, -49.99) * mm});
            skArc(sketch, "E200.0", {"start": v(70, -49.99) * mm, "mid": v(69.02, -52.37) * mm, "end": v(66.64, -53.35) * mm});
            skLineSegment(sketch, "E201.0", {"start": v(66.64, -53.35) * mm, "end": v(20, -53.35) * mm});
            skLineSegment(sketch, "E202.0", {"start": v(-66.64, -53.35) * mm, "end": v(-20, -53.35) * mm});
            skArc(sketch, "E203.0", {"start": v(-66.64, -53.35) * mm, "mid": v(-69.02, -52.37) * mm, "end": v(-70, -49.99) * mm});
            skLineSegment(sketch, "E204.0", {"start": v(-70, -32.83) * mm, "end": v(-70, -49.99) * mm});
            skArc(sketch, "E205.0", {"start": v(-70, -32.83) * mm, "mid": v(-69.46, -29.43) * mm, "end": v(-67.9, -26.36) * mm});
            skLineSegment(sketch, "E206.0", {"start": v(-58, -12.75) * mm, "end": v(-67.9, -26.36) * mm});
            skLineSegment(sketch, "E207.0", {"start": v(-58, 12.75) * mm, "end": v(-58, -12.75) * mm});
            skLineSegment(sketch, "E208.0", {"start": v(-67.6, 26.95) * mm, "end": v(-58, 12.75) * mm});
            skArc(sketch, "E209.0", {"start": v(-70, 34.79) * mm, "mid": v(-69.39, 30.69) * mm, "end": v(-67.6, 26.95) * mm});
            skLineSegment(sketch, "E210", {"start": v(70, 34.79) * mm, "end": v(67.5, 51.95) * mm});
            skLineSegment(sketch, "E211", {"start": v(-67.5, 51.95) * mm, "end": v(-70, 34.79) * mm});
            skLineSegment(sketch, "E212", {"start": v(20, -53.35) * mm, "end": v(-20, -53.35) * mm});
            skLineSegment(sketch, "E213", {"start": v(-67.5, 51.95) * mm, "end": v(-67.5, 104.82) * mm, "construction": true});
            skLineSegment(sketch, "E214", {"start": v(24.5, 117.85) * mm, "end": v(-24.5, 117.85) * mm, "construction": true});
            skLineSegment(sketch, "E215", {"start": v(26, 113.35) * mm, "end": v(24.5, 117.85) * mm});
            skLineSegment(sketch, "E216", {"start": v(-24.5, 117.85) * mm, "end": v(-26, 113.35) * mm});
            skArc(sketch, "E217", {"start": v(24.5, 117.85) * mm, "mid": v(22.7, 122.21) * mm, "end": v(18.33, 124.02) * mm});
            skArc(sketch, "E218.MirrorCS", {"start": v(-24.5, 117.85) * mm, "mid": v(-22.7, 122.21) * mm, "end": v(-18.33, 124.02) * mm});
            skLineSegment(sketch, "E219", {"start": v(18.33, 124.02) * mm, "end": v(-18.33, 124.02) * mm});
            skSolve(sketch);
        }
        {
            var Q0;
            Q0=qSketchRegion(id+"F28",true);
            extrude(context, id + "F29", {"entities" : qUnion([Q0]), "depth" : 6.35 * mm});
        }
        {
            var Q0;
            Q0=makeQuery(id+"F29.opExtrude","CAP_FACE",FACE,{"disambiguationData":[OSD([sQuery(id+"F28.wireOp",EDGE,"Hsz0tEu8-2u2z-894v-u5uz-qeEPLO7T1y3h"),sQuery(id+"F28.wireOp",EDGE,"vEOOrqZs-7KoW-orxh-Vkwo-SEQycOVZhe9Y"),sQuery(id+"F28.wireOp",EDGE,"aVo1oUrC-5gOD-S3Gd-KdpA-WAxqIndI85XZ"),sQuery(id+"F28.wireOp",EDGE,"9HF069ls-R4vM-rCiR-Mglt-uF1vui31pR4p"),sQuery(id+"F28.wireOp",EDGE,"6UwIWVSN-CBoj-eV2b-T7fp-u49lRc933uwu"),sQuery(id+"F28.wireOp",EDGE,"xATdj4HU-5i3P-5F5E-4dWz-QLdLokjUGgyJ"),sQuery(id+"F28.wireOp",EDGE,"E182"),sQuery(id+"F28.wireOp",EDGE,"E183"),sQuery(id+"F28.wireOp",EDGE,"E184"),sQuery(id+"F28.wireOp",EDGE,"E185"),sQuery(id+"F28.wireOp",EDGE,"E186"),sQuery(id+"F28.wireOp",EDGE,"01ed5a7f-363f-42f9-805d-97d743e7f8c00.MirrorCS"),sQuery(id+"F28.wireOp",EDGE,"E188.MirrorCS"),sQuery(id+"F28.wireOp",EDGE,"E189.MirrorCS"),sQuery(id+"F28.wireOp",EDGE,"E190.MirrorCS"),sQuery(id+"F28.wireOp",EDGE,"E191.MirrorCS"),sQuery(id+"F28.wireOp",EDGE,"E192.MirrorCS"),sQuery(id+"F28.wireOp",EDGE,"01ed5a7f-363f-42f9-805d-97d743e7f8c06.MirrorCS"),sQuery(id+"F28.wireOp",EDGE,"01ed5a7f-363f-42f9-805d-97d743e7f8c08.MirrorCS"),sQuery(id+"F28.wireOp",EDGE,"01ed5a7f-363f-42f9-805d-97d743e7f8c09.MirrorCS"),sQuery(id+"F28.wireOp",EDGE,"orUJIb6K-YDtt-LamK-tEY8-xfgMmjDqjYYe"),sQuery(id+"F28.wireOp",EDGE,"c8cb6b1b-2073-4661-974d-9f2328fd6722"),sQuery(id+"F28.wireOp",EDGE,"7cc86124-f559-48ea-aabb-f436df0639fe0.MirrorCS"),sQuery(id+"F28.wireOp",EDGE,"7cc86124-f559-48ea-aabb-f436df0639fe1.MirrorCS")])],"isStart":true});
            var sketch = newSketch(context, id + "F30", { "sketchPlane" : qUnion([Q0])});
            skCircle(sketch, "E220.0", {"center": v(-57, 39.7) * mm, "radius": 2.5 * mm});
            skCircle(sketch, "E221.0", {"center": v(-32, 39.7) * mm, "radius": 2.5 * mm});
            skCircle(sketch, "E222.0", {"center": v(32, 39.7) * mm, "radius": 2.5 * mm});
            skCircle(sketch, "E223.0", {"center": v(57, 39.7) * mm, "radius": 2.5 * mm});
            skCircle(sketch, "E224.0", {"center": v(-57, -40.1) * mm, "radius": 3.57 * mm});
            skCircle(sketch, "E225.0", {"center": v(57, -40.1) * mm, "radius": 3.57 * mm});
            skSolve(sketch);
        }
        {
            var Q0;
            Q0=qSketchRegion(id+"F30",true);
            extrude(context, id + "F31", {"entities" : qUnion([Q0]), "operationType" : NewBodyOperationType.REMOVE, "endBound" : BoundingType.THROUGH_ALL, "oppositeDirection" : true, "depth" : 25 * mm});
        }
        {
            var Q0;
            Q0=makeQuery(id+"F29.opExtrude","SWEPT_EDGE",EDGE,{"disambiguationData":[OSD([sQuery(id+"F28.wireOp",EDGE,"E183"),sQuery(id+"F28.wireOp",EDGE,"E184")])]});
            var Q1;
            Q1=makeQuery(id+"F29.opExtrude","SWEPT_EDGE",EDGE,{"disambiguationData":[OSD([sQuery(id+"F28.wireOp",EDGE,"E190.MirrorCS"),sQuery(id+"F28.wireOp",EDGE,"E191.MirrorCS")])]});
            fillet(context, id + "F32", {"entities" : qUnion([Q0, Q1]), "radius" : 13.7 * mm, "tangentPropagation" : true, "allowEdgeOverflow" : false});
        }
        {
            var Q0;
            Q0=makeQuery(id+"F29.opExtrude","SWEPT_EDGE",EDGE,{"disambiguationData":[OSD([sQuery(id+"F28.wireOp",EDGE,"E182"),sQuery(id+"F28.wireOp",EDGE,"E211")])]});
            var Q1;
            Q1=makeQuery(id+"F29.opExtrude","SWEPT_EDGE",EDGE,{"disambiguationData":[OSD([sQuery(id+"F28.wireOp",EDGE,"E192.MirrorCS"),sQuery(id+"F28.wireOp",EDGE,"E210")])]});
            fillet(context, id + "F33", {"entities" : qUnion([Q0, Q1]), "radius" : 5.5 * mm, "tangentPropagation" : true, "allowEdgeOverflow" : false});
        }
        {
            var Q0;
            Q0=makeQuery(id+"F29.opExtrude","CAP_FACE",FACE,{"disambiguationData":[OSD([sQuery(id+"F28.wireOp",EDGE,"E182"),sQuery(id+"F28.wireOp",EDGE,"E183"),sQuery(id+"F28.wireOp",EDGE,"E184"),sQuery(id+"F28.wireOp",EDGE,"E185"),sQuery(id+"F28.wireOp",EDGE,"E186"),sQuery(id+"F28.wireOp",EDGE,"E188.MirrorCS"),sQuery(id+"F28.wireOp",EDGE,"E189.MirrorCS"),sQuery(id+"F28.wireOp",EDGE,"E190.MirrorCS"),sQuery(id+"F28.wireOp",EDGE,"E191.MirrorCS"),sQuery(id+"F28.wireOp",EDGE,"E192.MirrorCS"),sQuery(id+"F28.wireOp",EDGE,"E194.0"),sQuery(id+"F28.wireOp",EDGE,"E195.0"),sQuery(id+"F28.wireOp",EDGE,"E196.0"),sQuery(id+"F28.wireOp",EDGE,"E197.0"),sQuery(id+"F28.wireOp",EDGE,"E198.0"),sQuery(id+"F28.wireOp",EDGE,"E199.0"),sQuery(id+"F28.wireOp",EDGE,"E200.0"),sQuery(id+"F28.wireOp",EDGE,"E201.0"),sQuery(id+"F28.wireOp",EDGE,"E202.0"),sQuery(id+"F28.wireOp",EDGE,"E203.0"),sQuery(id+"F28.wireOp",EDGE,"E204.0"),sQuery(id+"F28.wireOp",EDGE,"E205.0"),sQuery(id+"F28.wireOp",EDGE,"E206.0"),sQuery(id+"F28.wireOp",EDGE,"E207.0"),sQuery(id+"F28.wireOp",EDGE,"E208.0"),sQuery(id+"F28.wireOp",EDGE,"E209.0"),sQuery(id+"F28.wireOp",EDGE,"E210"),sQuery(id+"F28.wireOp",EDGE,"E211"),sQuery(id+"F28.wireOp",EDGE,"E212")])],"isStart":true});
            var sketch = newSketch(context, id + "F34", { "sketchPlane" : qUnion([Q0])});
            skLineSegment(sketch, "E226.bottom", {"start": v(-19.85, 29.35) * mm, "end": v(19.85, 29.35) * mm});
            skLineSegment(sketch, "E226.top", {"start": v(-19.85, -28.35) * mm, "end": v(19.85, -28.35) * mm});
            skLineSegment(sketch, "E226.left", {"start": v(-35.85, 13.35) * mm, "end": v(-35.85, -12.35) * mm});
            skLineSegment(sketch, "E226.right", {"start": v(35.85, 13.35) * mm, "end": v(35.85, -12.35) * mm});
            skLineSegment(sketch, "E227", {"start": v(0, 29.35) * mm, "end": v(0, 0) * mm, "construction": true});
            skLineSegment(sketch, "E228", {"start": v(0, 0) * mm, "end": v(0, -28.35) * mm, "construction": true});
            skPoint(sketch, "E229.visualSharp", {"position": v(-35.85, 29.35) * mm});
            skArc(sketch, "E229.filletArc", {"start": v(-19.85, 29.35) * mm, "mid": v(-31.16, 24.66) * mm, "end": v(-35.85, 13.35) * mm});
            skPoint(sketch, "E230.visualSharp", {"position": v(35.85, 29.35) * mm});
            skArc(sketch, "E230.filletArc", {"start": v(35.85, 13.35) * mm, "mid": v(31.16, 24.66) * mm, "end": v(19.85, 29.35) * mm});
            skPoint(sketch, "E231.visualSharp", {"position": v(35.85, -28.35) * mm});
            skArc(sketch, "E231.filletArc", {"start": v(19.85, -28.35) * mm, "mid": v(31.16, -23.66) * mm, "end": v(35.85, -12.35) * mm});
            skPoint(sketch, "E232.visualSharp", {"position": v(-35.85, -28.35) * mm});
            skArc(sketch, "E232.filletArc", {"start": v(-35.85, -12.35) * mm, "mid": v(-31.16, -23.66) * mm, "end": v(-19.85, -28.35) * mm});
            skSolve(sketch);
        }
        {
            var Q0;
            Q0=qSketchRegion(id+"F34",true);
            extrude(context, id + "F35", {"entities" : qUnion([Q0]), "operationType" : NewBodyOperationType.REMOVE, "endBound" : BoundingType.THROUGH_ALL, "oppositeDirection" : true, "depth" : 25 * mm});
        }
        {
            var Q0;
            Q0=makeQuery(id+"F29.opExtrude","CAP_FACE",FACE,{"disambiguationData":[OSD([sQuery(id+"F28.wireOp",EDGE,"E182"),sQuery(id+"F28.wireOp",EDGE,"E183"),sQuery(id+"F28.wireOp",EDGE,"E184"),sQuery(id+"F28.wireOp",EDGE,"E190.MirrorCS"),sQuery(id+"F28.wireOp",EDGE,"E191.MirrorCS"),sQuery(id+"F28.wireOp",EDGE,"E192.MirrorCS"),sQuery(id+"F28.wireOp",EDGE,"E194.0"),sQuery(id+"F28.wireOp",EDGE,"E195.0"),sQuery(id+"F28.wireOp",EDGE,"E196.0"),sQuery(id+"F28.wireOp",EDGE,"E197.0"),sQuery(id+"F28.wireOp",EDGE,"E198.0"),sQuery(id+"F28.wireOp",EDGE,"E199.0"),sQuery(id+"F28.wireOp",EDGE,"E200.0"),sQuery(id+"F28.wireOp",EDGE,"E201.0"),sQuery(id+"F28.wireOp",EDGE,"E202.0"),sQuery(id+"F28.wireOp",EDGE,"E203.0"),sQuery(id+"F28.wireOp",EDGE,"E204.0"),sQuery(id+"F28.wireOp",EDGE,"E205.0"),sQuery(id+"F28.wireOp",EDGE,"E206.0"),sQuery(id+"F28.wireOp",EDGE,"E207.0"),sQuery(id+"F28.wireOp",EDGE,"E208.0"),sQuery(id+"F28.wireOp",EDGE,"E209.0"),sQuery(id+"F28.wireOp",EDGE,"E210"),sQuery(id+"F28.wireOp",EDGE,"E211"),sQuery(id+"F28.wireOp",EDGE,"E212"),sQuery(id+"F28.wireOp",EDGE,"E215"),sQuery(id+"F28.wireOp",EDGE,"E216"),sQuery(id+"F28.wireOp",EDGE,"E217"),sQuery(id+"F28.wireOp",EDGE,"E218.MirrorCS"),sQuery(id+"F28.wireOp",EDGE,"E219")])],"isStart":true});
            var sketch = newSketch(context, id + "F36", { "sketchPlane" : qUnion([Q0])});
            skLineSegment(sketch, "E233", {"start": v(0, 29.35) * mm, "end": v(0, 124.02) * mm, "construction": true});
            skLineSegment(sketch, "E234", {"start": v(-3.5, 121.02) * mm, "end": v(-6.5, 124.02) * mm});
            skArc(sketch, "E235", {"start": v(-3.5, 121.02) * mm, "mid": v(-3.6, 119.52) * mm, "end": v(-5.08, 119.82) * mm});
            skLineSegment(sketch, "E236", {"start": v(-5.08, 119.82) * mm, "end": v(-7.5, 119.82) * mm});
            skArc(sketch, "E237", {"start": v(-7.5, 119.82) * mm, "mid": v(-11.5, 115.82) * mm, "end": v(-7.5, 111.82) * mm});
            skLineSegment(sketch, "E238", {"start": v(-7.5, 111.82) * mm, "end": v(0, 111.82) * mm});
            skLineSegment(sketch, "E239", {"start": v(-6.5, 124.02) * mm, "end": v(0, 124.02) * mm});
            skLineSegment(sketch, "E240.MirrorCS", {"start": v(7.5, 111.82) * mm, "end": v(0, 111.82) * mm});
            skArc(sketch, "E241.MirrorCS", {"start": v(7.5, 119.82) * mm, "mid": v(11.5, 115.82) * mm, "end": v(7.5, 111.82) * mm});
            skLineSegment(sketch, "E242.MirrorCS", {"start": v(5.08, 119.82) * mm, "end": v(7.5, 119.82) * mm});
            skArc(sketch, "E243.MirrorCS", {"start": v(3.5, 121.02) * mm, "mid": v(3.6, 119.52) * mm, "end": v(5.08, 119.82) * mm});
            skLineSegment(sketch, "E244.MirrorCS", {"start": v(3.5, 121.02) * mm, "end": v(6.5, 124.02) * mm});
            skLineSegment(sketch, "E245.MirrorCS", {"start": v(6.5, 124.02) * mm, "end": v(0, 124.02) * mm});
            skLineSegment(sketch, "E246", {"start": v(-7.5, 115.82) * mm, "end": v(-17.86, 115.82) * mm, "construction": true});
            skPoint(sketch, "E246.endSnap0", {"position": v(-11.5, 115.82) * mm});
            skCircle(sketch, "E247", {"center": v(-17.86, 115.82) * mm, "radius": 2.7 * mm});
            skLineSegment(sketch, "E248.MirrorCS", {"start": v(7.5, 115.82) * mm, "end": v(17.86, 115.82) * mm, "construction": true});
            skCircle(sketch, "E249.MirrorC", {"center": v(17.86, 115.82) * mm, "radius": 2.7 * mm});
            skSolve(sketch);
        }
        {
            var Q0;
            Q0=qSketchRegion(id+"F36",true);
            extrude(context, id + "F37", {"entities" : qUnion([Q0]), "operationType" : NewBodyOperationType.REMOVE, "endBound" : BoundingType.THROUGH_ALL, "oppositeDirection" : true, "depth" : 25 * mm});
        }
        {
            var Q0;
            Q0=makeQuery(id+"F29.opExtrude","CAP_FACE",FACE,{"disambiguationData":[OSD([sQuery(id+"F28.wireOp",EDGE,"E182"),sQuery(id+"F28.wireOp",EDGE,"E183"),sQuery(id+"F28.wireOp",EDGE,"E184"),sQuery(id+"F28.wireOp",EDGE,"E190.MirrorCS"),sQuery(id+"F28.wireOp",EDGE,"E191.MirrorCS"),sQuery(id+"F28.wireOp",EDGE,"E192.MirrorCS"),sQuery(id+"F28.wireOp",EDGE,"E194.0"),sQuery(id+"F28.wireOp",EDGE,"E195.0"),sQuery(id+"F28.wireOp",EDGE,"E196.0"),sQuery(id+"F28.wireOp",EDGE,"E197.0"),sQuery(id+"F28.wireOp",EDGE,"E198.0"),sQuery(id+"F28.wireOp",EDGE,"E199.0"),sQuery(id+"F28.wireOp",EDGE,"E200.0"),sQuery(id+"F28.wireOp",EDGE,"E201.0"),sQuery(id+"F28.wireOp",EDGE,"E202.0"),sQuery(id+"F28.wireOp",EDGE,"E203.0"),sQuery(id+"F28.wireOp",EDGE,"E204.0"),sQuery(id+"F28.wireOp",EDGE,"E205.0"),sQuery(id+"F28.wireOp",EDGE,"E206.0"),sQuery(id+"F28.wireOp",EDGE,"E207.0"),sQuery(id+"F28.wireOp",EDGE,"E208.0"),sQuery(id+"F28.wireOp",EDGE,"E209.0"),sQuery(id+"F28.wireOp",EDGE,"E210"),sQuery(id+"F28.wireOp",EDGE,"E211"),sQuery(id+"F28.wireOp",EDGE,"E212"),sQuery(id+"F28.wireOp",EDGE,"E215"),sQuery(id+"F28.wireOp",EDGE,"E216"),sQuery(id+"F28.wireOp",EDGE,"E217"),sQuery(id+"F28.wireOp",EDGE,"E218.MirrorCS"),sQuery(id+"F28.wireOp",EDGE,"E219")])],"isStart":true});
            var sketch = newSketch(context, id + "F38", { "sketchPlane" : qUnion([Q0])});
            skLineSegment(sketch, "E250", {"start": v(0, 0) * mm, "end": v(0, 71.97) * mm, "construction": true});
            skLineSegment(sketch, "E251", {"start": v(0, 71.97) * mm, "end": v(0, 81.97) * mm, "construction": true});
            skLineSegment(sketch, "E252", {"start": v(0, 81.97) * mm, "end": v(0, 111.82) * mm, "construction": true});
            skArc(sketch, "E253", {"start": v(-12.5, 81.97) * mm, "mid": v(0, 94.47) * mm, "end": v(12.5, 81.97) * mm});
            skArc(sketch, "E254", {"start": v(-12.5, 71.97) * mm, "mid": v(0, 59.47) * mm, "end": v(12.5, 71.97) * mm});
            skLineSegment(sketch, "E255", {"start": v(-12.5, 81.97) * mm, "end": v(-12.5, 71.97) * mm});
            skLineSegment(sketch, "E256", {"start": v(12.5, 81.97) * mm, "end": v(12.5, 71.97) * mm});
            skLineSegment(sketch, "E257", {"start": v(-23.57, 100.54) * mm, "end": v(0, 100.54) * mm, "construction": true});
            skLineSegment(sketch, "E258", {"start": v(0, 100.54) * mm, "end": v(23.57, 100.54) * mm, "construction": true});
            skLineSegment(sketch, "E259", {"start": v(23.57, 100.54) * mm, "end": v(0, 76.97) * mm, "construction": true});
            skLineSegment(sketch, "E260", {"start": v(0, 76.97) * mm, "end": v(-23.57, 53.4) * mm, "construction": true});
            skLineSegment(sketch, "E261", {"start": v(-23.57, 53.4) * mm, "end": v(0, 53.4) * mm, "construction": true});
            skLineSegment(sketch, "E262", {"start": v(0, 53.4) * mm, "end": v(23.57, 53.4) * mm, "construction": true});
            skLineSegment(sketch, "E263", {"start": v(23.57, 53.4) * mm, "end": v(0, 76.97) * mm, "construction": true});
            skLineSegment(sketch, "E264", {"start": v(0, 76.97) * mm, "end": v(-23.57, 100.54) * mm, "construction": true});
            skLineSegment(sketch, "E265", {"start": v(-23.57, 105.04) * mm, "end": v(-23.57, 96.04) * mm, "construction": true});
            skLineSegment(sketch, "E266", {"start": v(23.57, 105.04) * mm, "end": v(23.57, 96.04) * mm, "construction": true});
            skLineSegment(sketch, "E267", {"start": v(0, 76.97) * mm, "end": v(-12.5, 76.97) * mm, "construction": true});
            skLineSegment(sketch, "E268", {"start": v(-23.57, 57.9) * mm, "end": v(-23.57, 48.9) * mm, "construction": true});
            skLineSegment(sketch, "E269", {"start": v(23.57, 57.9) * mm, "end": v(23.57, 48.9) * mm, "construction": true});
            skArc(sketch, "E270", {"start": v(-26.07, 57.9) * mm, "mid": v(-23.57, 60.4) * mm, "end": v(-21.07, 57.9) * mm});
            skArc(sketch, "E271", {"start": v(-26.07, 48.9) * mm, "mid": v(-23.57, 46.4) * mm, "end": v(-21.07, 48.9) * mm});
            skLineSegment(sketch, "E272", {"start": v(-26.07, 57.9) * mm, "end": v(-26.07, 48.9) * mm});
            skLineSegment(sketch, "E273", {"start": v(-21.07, 57.9) * mm, "end": v(-21.07, 48.9) * mm});
            skArc(sketch, "E274.MirrorCS", {"start": v(26.07, 57.9) * mm, "mid": v(23.57, 60.4) * mm, "end": v(21.07, 57.9) * mm});
            skLineSegment(sketch, "E275.MirrorCS", {"start": v(26.07, 57.9) * mm, "end": v(26.07, 48.9) * mm});
            skLineSegment(sketch, "E276.MirrorCS", {"start": v(21.07, 57.9) * mm, "end": v(21.07, 48.9) * mm});
            skArc(sketch, "E277.MirrorCS", {"start": v(26.07, 48.9) * mm, "mid": v(23.57, 46.4) * mm, "end": v(21.07, 48.9) * mm});
            skLineSegment(sketch, "E278.MirrorCS", {"start": v(-26.07, 96.04) * mm, "end": v(-26.07, 105.04) * mm});
            skArc(sketch, "E279.MirrorCS", {"start": v(-26.07, 96.04) * mm, "mid": v(-23.57, 93.54) * mm, "end": v(-21.07, 96.04) * mm});
            skLineSegment(sketch, "E280.MirrorCS", {"start": v(-21.07, 96.04) * mm, "end": v(-21.07, 105.04) * mm});
            skArc(sketch, "E281.MirrorCS", {"start": v(-26.07, 105.04) * mm, "mid": v(-23.57, 107.54) * mm, "end": v(-21.07, 105.04) * mm});
            skArc(sketch, "E282.MirrorCS", {"start": v(26.07, 105.04) * mm, "mid": v(23.57, 107.54) * mm, "end": v(21.07, 105.04) * mm});
            skLineSegment(sketch, "E283.MirrorCS", {"start": v(21.07, 96.04) * mm, "end": v(21.07, 105.04) * mm});
            skArc(sketch, "E284.MirrorCS", {"start": v(26.07, 96.04) * mm, "mid": v(23.57, 93.54) * mm, "end": v(21.07, 96.04) * mm});
            skLineSegment(sketch, "E285.MirrorCS", {"start": v(26.07, 96.04) * mm, "end": v(26.07, 105.04) * mm});
            skSolve(sketch);
        }
        {
            var Q0;
            Q0=qSketchRegion(id+"F38",true);
            extrude(context, id + "F39", {"entities" : qUnion([Q0]), "operationType" : NewBodyOperationType.REMOVE, "endBound" : BoundingType.THROUGH_ALL, "oppositeDirection" : true, "depth" : 25 * mm});
        }
    });
